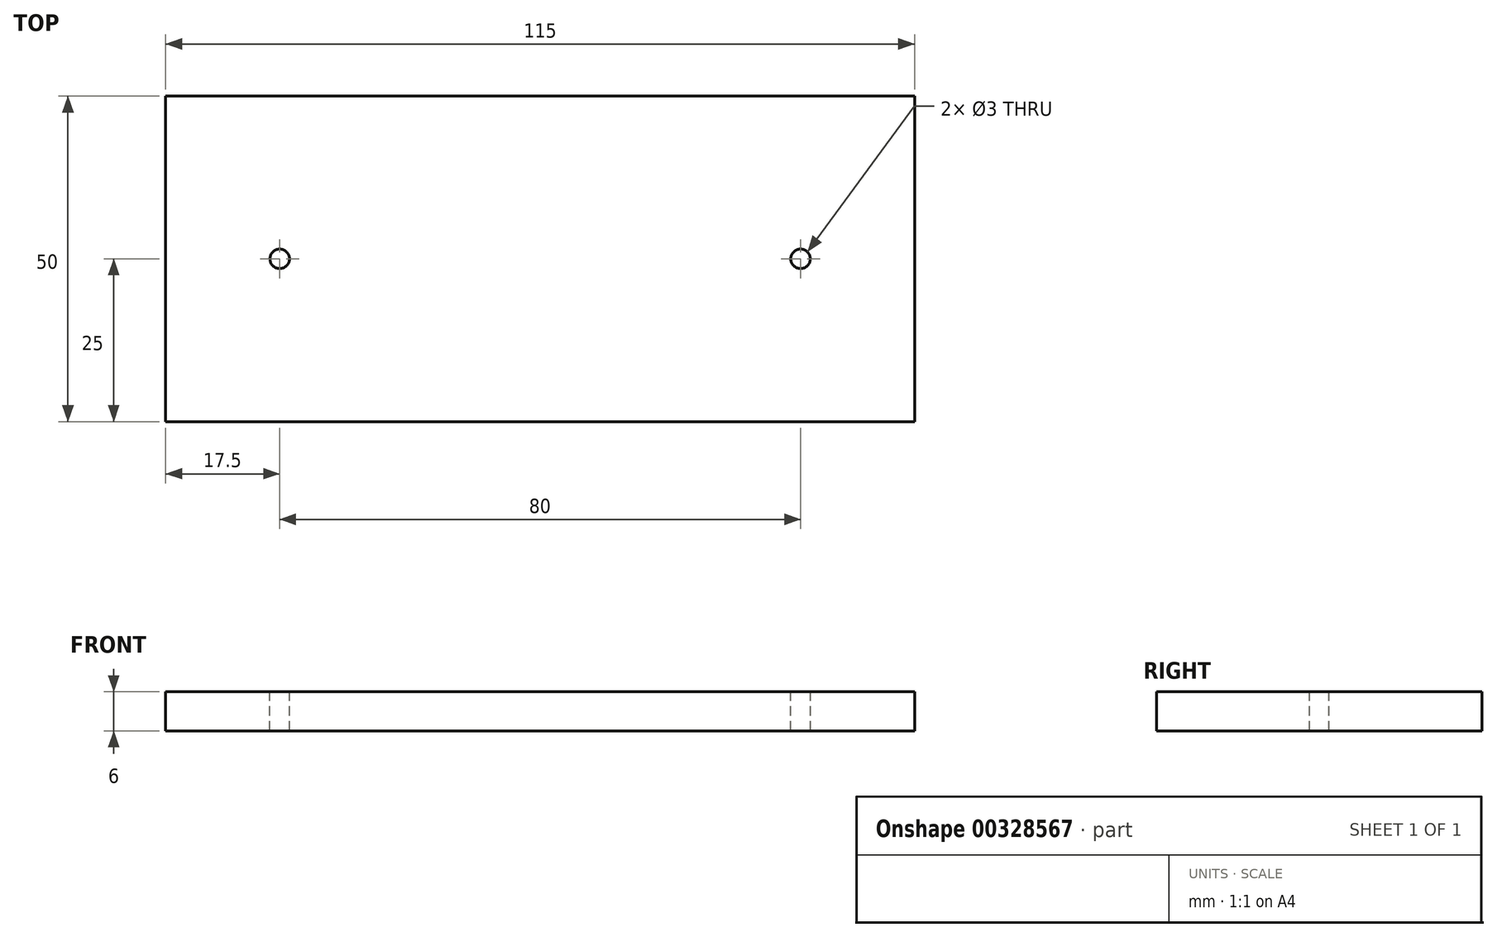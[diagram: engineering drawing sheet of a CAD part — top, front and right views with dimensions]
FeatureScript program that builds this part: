
annotation { "Feature Type Name" : "Feature", "Feature Type Description" : "" }
export const myFeature = defineFeature(function(context is Context, id is Id, definition is map)
    precondition{}
    {
        {
            var Q0;
            Q0=qCreatedBy(makeId("Top.planeOp"),FACE);
            var sketch = newSketch(context, id + "F0", { "sketchPlane" : qUnion([Q0])});
            skLineSegment(sketch, "E0.bottom", {"start": v(57.5, 25) * mm, "end": v(-57.5, 25) * mm});
            skLineSegment(sketch, "E0.top", {"start": v(57.5, -25) * mm, "end": v(-57.5, -25) * mm});
            skLineSegment(sketch, "E0.left", {"start": v(57.5, 25) * mm, "end": v(57.5, -25) * mm});
            skLineSegment(sketch, "E0.right", {"start": v(-57.5, 25) * mm, "end": v(-57.5, -25) * mm});
            skPoint(sketch, "E0.middle", {"position": v(0, 0) * mm});
            skSolve(sketch);
        }
        {
            var Q0;
            Q0 = qSketchRegion(id + "F0", true);
            extrude(context, id + "F1", {"entities" : qUnion([Q0]), "depth" : 6 * mm});
        }
        {
            var Q0;
            Q0=makeQuery(id+"F1.opExtrude","CAP_FACE",FACE,{"disambiguationData":[OSD([sQuery(id+"F0.wireOp",EDGE,"E0.bottom"),sQuery(id+"F0.wireOp",EDGE,"E0.top"),sQuery(id+"F0.wireOp",EDGE,"E0.left"),sQuery(id+"F0.wireOp",EDGE,"E0.right")])],"isStart":false});
            var sketch = newSketch(context, id + "F2", { "sketchPlane" : qUnion([Q0])});
            skCircle(sketch, "E1", {"center": v(-40, 0) * mm, "radius": 1.5 * mm});
            skCircle(sketch, "E2", {"center": v(40, 0) * mm, "radius": 1.5 * mm});
            skLineSegment(sketch, "E3", {"start": v(0, 0) * mm, "end": v(0, 33.26) * mm, "construction": true});
            skSolve(sketch);
        }
        {
            var Q0;
            Q0 = qSketchRegion(id + "F2", true);
            extrude(context, id + "F3", {"entities" : qUnion([Q0]), "operationType" : NewBodyOperationType.REMOVE, "endBound" : BoundingType.THROUGH_ALL, "oppositeDirection" : true, "depth" : 25 * mm});
        }
    });
